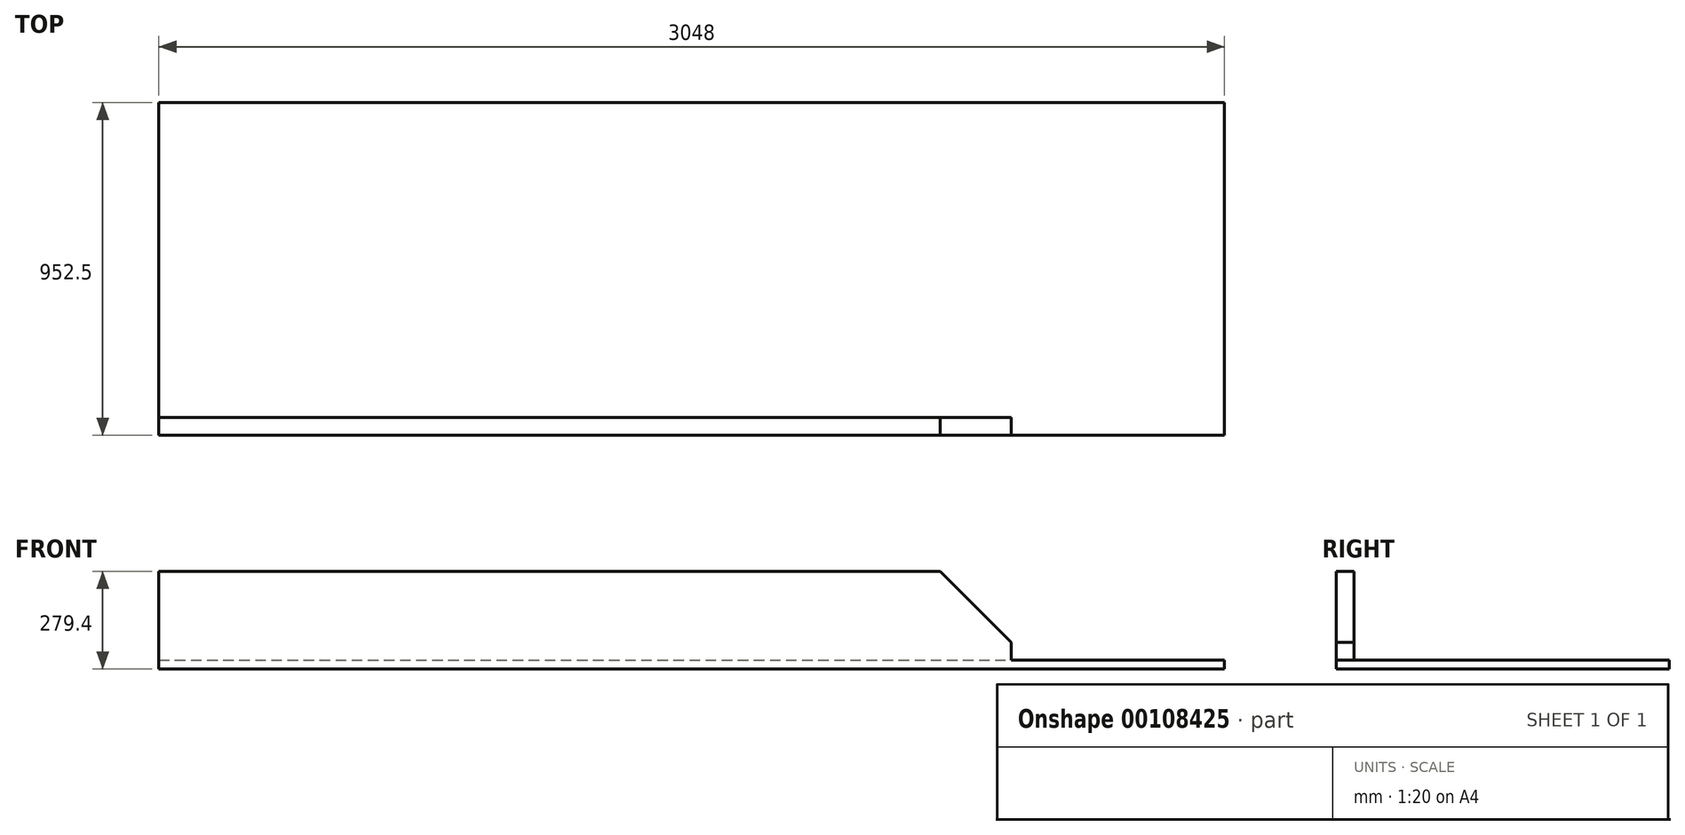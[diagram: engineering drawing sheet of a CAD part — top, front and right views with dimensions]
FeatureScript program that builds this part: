
annotation { "Feature Type Name" : "Feature", "Feature Type Description" : "" }
export const myFeature = defineFeature(function(context is Context, id is Id, definition is map)
    precondition{}
    {
        {
            var Q0;
            Q0=qCreatedBy(makeId("Top.planeOp"),FACE);
            var sketch = newSketch(context, id + "F0", { "sketchPlane" : qUnion([Q0])});
            skLineSegment(sketch, "E0.bottom", {"start": v(0, 0) * mm, "end": v(3048, 0) * mm});
            skLineSegment(sketch, "E0.top", {"start": v(0, 952.5) * mm, "end": v(3048, 952.5) * mm});
            skLineSegment(sketch, "E0.left", {"start": v(0, 0) * mm, "end": v(0, 952.5) * mm});
            skLineSegment(sketch, "E0.right", {"start": v(3048, 0) * mm, "end": v(3048, 952.5) * mm});
            skSolve(sketch);
        }
        {
            var Q0;
            Q0=qSketchRegion(id+"F0",true);
            extrude(context, id + "F1", {"entities" : qUnion([Q0]), "depth" : 25.4 * mm});
        }
        {
            var Q0;
            Q0=makeQuery(id+"F1.opExtrude","SWEPT_FACE",FACE,{"disambiguationData":[OSD([sQuery(id+"F0.wireOp",EDGE,"E0.bottom")])]});
            var sketch = newSketch(context, id + "F2", { "sketchPlane" : qUnion([Q0])});
            skLineSegment(sketch, "E1.bottom", {"start": v(0, 25.4) * mm, "end": v(2438.4, 25.4) * mm});
            skLineSegment(sketch, "E1.top", {"start": v(0, 279.4) * mm, "end": v(2438.4, 279.4) * mm});
            skLineSegment(sketch, "E1.left", {"start": v(0, 25.4) * mm, "end": v(0, 279.4) * mm});
            skLineSegment(sketch, "E1.right", {"start": v(2438.4, 25.4) * mm, "end": v(2438.4, 279.4) * mm});
            skSolve(sketch);
        }
        {
            var Q0;
            Q0=qSketchRegion(id+"F2",true);
            extrude(context, id + "F3", {"entities" : qUnion([Q0]), "operationType" : NewBodyOperationType.ADD, "oppositeDirection" : true, "depth" : 50.8 * mm});
        }
        {
            var Q0;
            Q0=makeQuery(id+"F3.opExtrude","SWEPT_EDGE",EDGE,{"disambiguationData":[OSD([sQuery(id+"F2.wireOp",EDGE,"E1.top"),sQuery(id+"F2.wireOp",EDGE,"E1.right")])]});
            chamfer(context, id + "F4", {"entities" : qUnion([Q0]), "width" : 203.2 * mm, "tangentPropagation" : true});
        }
    });
